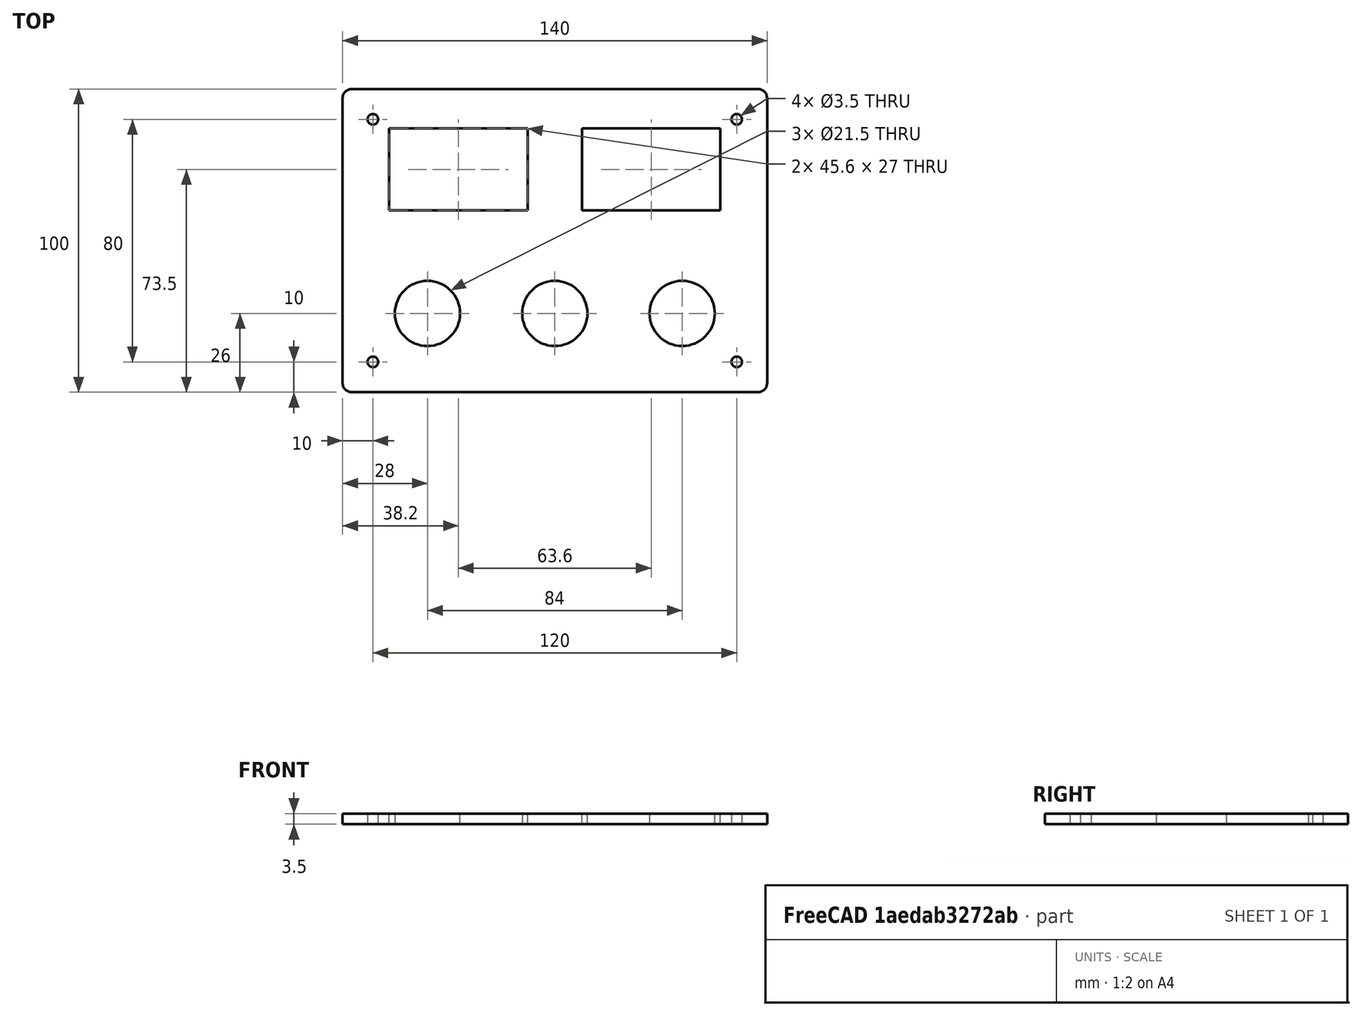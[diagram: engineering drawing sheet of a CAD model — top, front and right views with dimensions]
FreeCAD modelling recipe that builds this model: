
FCSTD DOCUMENT  (FreeCAD 0.21R33771 (Git))
Label: пластина управления питанием
License: All rights reserved
LicenseURL: https://en.wikipedia.org/wiki/All_rights_reserved
objects: Sketcher::SketchObject×1, PartDesign::Pad×1, PartDesign::Body×1
note: 4 computed .brp shape members not serialized (recipe doc carries the construction recipe); baked Part::Feature solids carry a one-line shape summary decoded from their .brp

FEATURE [Sketcher::SketchObject] Sketch
  FullyConstrained = true
  MapMode = 5
  Support = -> [XY_Plane]
  sketch-geometry (27):
    g0: LineSegment StartX=-67 StartY=50 StartZ=0 EndX=67 EndY=50 EndZ=0
    g1: LineSegment StartX=70 StartY=47 StartZ=0 EndX=70 EndY=-47 EndZ=0
    g2: LineSegment StartX=67 StartY=-50 StartZ=0 EndX=-67 EndY=-50 EndZ=0
    g3: LineSegment StartX=-70 StartY=-47 StartZ=0 EndX=-70 EndY=47 EndZ=0
    g4: Circle CenterX=-42 CenterY=-24 CenterZ=0 NormalX=0 NormalY=0 NormalZ=1 AngleXU=0 Radius=10.75
    g5: Circle CenterX=42 CenterY=-24 CenterZ=0 NormalX=0 NormalY=0 NormalZ=1 AngleXU=0 Radius=10.75
    g6: LineSegment StartX=-54.6 StartY=37 StartZ=0 EndX=-9 EndY=37 EndZ=0
    g7: LineSegment StartX=-9 StartY=37 StartZ=0 EndX=-9 EndY=10 EndZ=0
    g8: LineSegment StartX=-9 StartY=10 StartZ=0 EndX=-54.6 EndY=10 EndZ=0
    g9: LineSegment StartX=-54.6 StartY=10 StartZ=0 EndX=-54.6 EndY=37 EndZ=0
    g10: LineSegment StartX=9 StartY=37 StartZ=0 EndX=54.6 EndY=37 EndZ=0
    g11: LineSegment StartX=54.6 StartY=37 StartZ=0 EndX=54.6 EndY=10 EndZ=0
    g12: LineSegment StartX=54.6 StartY=10 StartZ=0 EndX=9 EndY=10 EndZ=0
    g13: LineSegment StartX=9 StartY=10 StartZ=0 EndX=9 EndY=37 EndZ=0
    g14: Circle CenterX=-60 CenterY=40 CenterZ=0 NormalX=0 NormalY=0 NormalZ=1 AngleXU=0 Radius=1.75
    g15: Circle CenterX=60 CenterY=40 CenterZ=0 NormalX=0 NormalY=0 NormalZ=1 AngleXU=0 Radius=1.75
    g16: Circle CenterX=-60 CenterY=-40 CenterZ=0 NormalX=0 NormalY=0 NormalZ=1 AngleXU=0 Radius=1.75
    g17: Circle CenterX=60 CenterY=-40 CenterZ=0 NormalX=0 NormalY=0 NormalZ=1 AngleXU=0 Radius=1.75
    g18: ArcOfCircle CenterX=67 CenterY=47 CenterZ=0 NormalX=0 NormalY=0 NormalZ=1 AngleXU=0 Radius=3 StartAngle=-9e-16 EndAngle=1.5708
    g19: GeomPoint X=70 Y=50 Z=0
    g20: ArcOfCircle CenterX=67 CenterY=-47 CenterZ=0 NormalX=0 NormalY=0 NormalZ=1 AngleXU=0 Radius=3 StartAngle=4.71239 EndAngle=6.28319
    g21: GeomPoint X=70 Y=-50 Z=0
    g22: ArcOfCircle CenterX=-67 CenterY=-47 CenterZ=0 NormalX=0 NormalY=0 NormalZ=1 AngleXU=0 Radius=3 StartAngle=3.14159 EndAngle=4.71239
    g23: GeomPoint X=-70 Y=-50 Z=0
    g24: ArcOfCircle CenterX=-67 CenterY=47 CenterZ=0 NormalX=0 NormalY=0 NormalZ=1 AngleXU=0 Radius=3 StartAngle=1.5708 EndAngle=3.14159
    g25: GeomPoint X=-70 Y=50 Z=0
    g26: Circle CenterX=0 CenterY=-24 CenterZ=0 NormalX=0 NormalY=0 NormalZ=1 AngleXU=0 Radius=10.75
  constraints (73):
    c: Horizontal(g0)
    c: Horizontal(g2)
    c: Vertical(g1)
    c: Vertical(g3)
    c: DistanceY(g23,g25) = 100
    c: DistanceX(g25,g19) = 140
    c: DistanceY(g-1,g25) = 50
    c: DistanceX(g25,g-1) = 70
    c: Diameter(g4) = 21.5
    c: DistanceX(g4,g-1) = 42
    c: DistanceY(g4,g-1) = 24
    c: Diameter(g5) = 21.5
    c: DistanceX(g-1,g5) = 42
    c: DistanceY(g5,g-1) = 24
    c: Coincident(g6,g7)
    c: Coincident(g7,g8)
    c: Coincident(g8,g9)
    c: Coincident(g9,g6)
    c: Horizontal(g6)
    c: Horizontal(g8)
    c: Vertical(g7)
    c: Vertical(g9)
    c: DistanceX(g6,g6) = 45.6
    c: DistanceY(g8,g6) = 27
    c: DistanceX(g6,g-1) = 9
    c: DistanceY(g-1,g8) = 10
    c: Coincident(g10,g11)
    c: Coincident(g11,g12)
    c: Coincident(g12,g13)
    c: Coincident(g13,g10)
    c: Horizontal(g10)
    c: Horizontal(g12)
    c: Vertical(g11)
    c: Vertical(g13)
    c: DistanceX(g10,g10) = 45.6
    c: DistanceY(g12,g10) = 27
    c: DistanceX(g-1,g10) = 9
    c: DistanceY(g-1,g12) = 10
    c: Diameter(g14) = 3.5
    c: DistanceY(g14,g25) = 10
    c: DistanceX(g25,g14) = 10
    c: Diameter(g15) = 3.5
    c: DistanceX(g15,g19) = 10
    c: DistanceY(g15,g19) = 10
    c: Diameter(g16) = 3.5
    c: DistanceY(g23,g16) = 10
    c: DistanceX(g23,g16) = 10
    c: Diameter(g17) = 3.5
    c: DistanceY(g21,g17) = 10
    c: DistanceX(g17,g21) = 10
    c: PointOnObject(g19,g0)
    c: PointOnObject(g19,g1)
    c: Tangent(g0,g18) = 1.5708
    c: Tangent(g1,g18) = 1.5708
    c: DistanceY(g18,g0) = 3
    c: PointOnObject(g21,g1)
    c: PointOnObject(g21,g2)
    c: Tangent(g1,g20) = 1.5708
    c: Tangent(g2,g20) = 1.5708
    c: DistanceX(g2,g21) = 3
    c: PointOnObject(g23,g3)
    c: PointOnObject(g23,g2)
    c: Tangent(g3,g22) = 1.5708
    c: Tangent(g2,g22) = 1.5708
    c: DistanceX(g23,g2) = 3
    c: PointOnObject(g25,g0)
    c: PointOnObject(g25,g3)
    c: Tangent(g0,g24) = 1.5708
    c: Tangent(g3,g24) = 1.5708
    c: DistanceX(g25,g0) = 3
    c: PointOnObject(g26,g-2)
    c: Diameter(g26) = 21.5
    c: DistanceY(g26,g-1) = 24
FEATURE [PartDesign::Pad] Pad
  Direction = (0,0,1)
  Length = 3.5
  Length2 = 10
  Profile = -> Sketch
  ReferenceAxis = -> Sketch [N_Axis]
  Type = 0
FEATURE [PartDesign::Body] Body
  Group = -> [Sketch,Pad]
  Origin = -> Origin
  Tip = -> Pad
